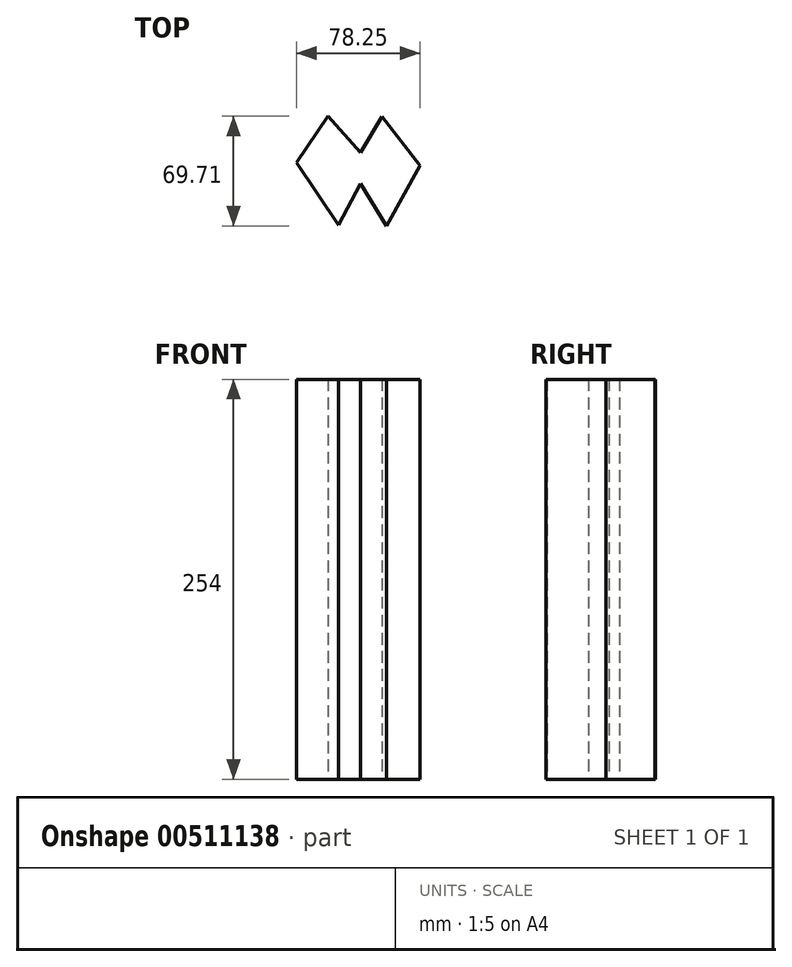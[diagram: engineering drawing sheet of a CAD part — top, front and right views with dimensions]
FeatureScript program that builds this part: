
annotation { "Feature Type Name" : "Feature", "Feature Type Description" : "" }
export const myFeature = defineFeature(function(context is Context, id is Id, definition is map)
    precondition{}
    {
        {
            var Q0;
            Q0=qCreatedBy(makeId("Top.planeOp"),FACE);
            var sketch = newSketch(context, id + "F0", { "sketchPlane" : qUnion([Q0])});
            skLineSegment(sketch, "E0", {"start": v(-40.64, 28) * mm, "end": v(-13.94, -11.58) * mm});
            skLineSegment(sketch, "E1", {"start": v(-13.94, -11.58) * mm, "end": v(0, 14.81) * mm});
            skLineSegment(sketch, "E2", {"start": v(0, 14.81) * mm, "end": v(16.44, -12.2) * mm});
            skLineSegment(sketch, "E3", {"start": v(16.44, -12.2) * mm, "end": v(37.61, 26.17) * mm});
            skLineSegment(sketch, "E4", {"start": v(37.61, 26.17) * mm, "end": v(13.68, 57.16) * mm});
            skLineSegment(sketch, "E5", {"start": v(13.68, 57.16) * mm, "end": v(0, 34.54) * mm});
            skLineSegment(sketch, "E6", {"start": v(0, 34.54) * mm, "end": v(-20.75, 57.52) * mm});
            skLineSegment(sketch, "E7", {"start": v(-20.75, 57.52) * mm, "end": v(-40.64, 28) * mm});
            skSolve(sketch);
        }
        {
            var Q0;
            Q0=makeQuery(id+"F0.imprint","IMPRINT",FACE,{"disambiguationData":[TD([[makeQuery(id+"F0.imprint","IMPRINT",EDGE,{"derivedFrom":sQuery(id+"F0.wireOp",EDGE,"E0")}),1.0]])]});
            extrude(context, id + "F1", {"entities" : qUnion([Q0]), "depth" : 254 * mm});
        }
    });
